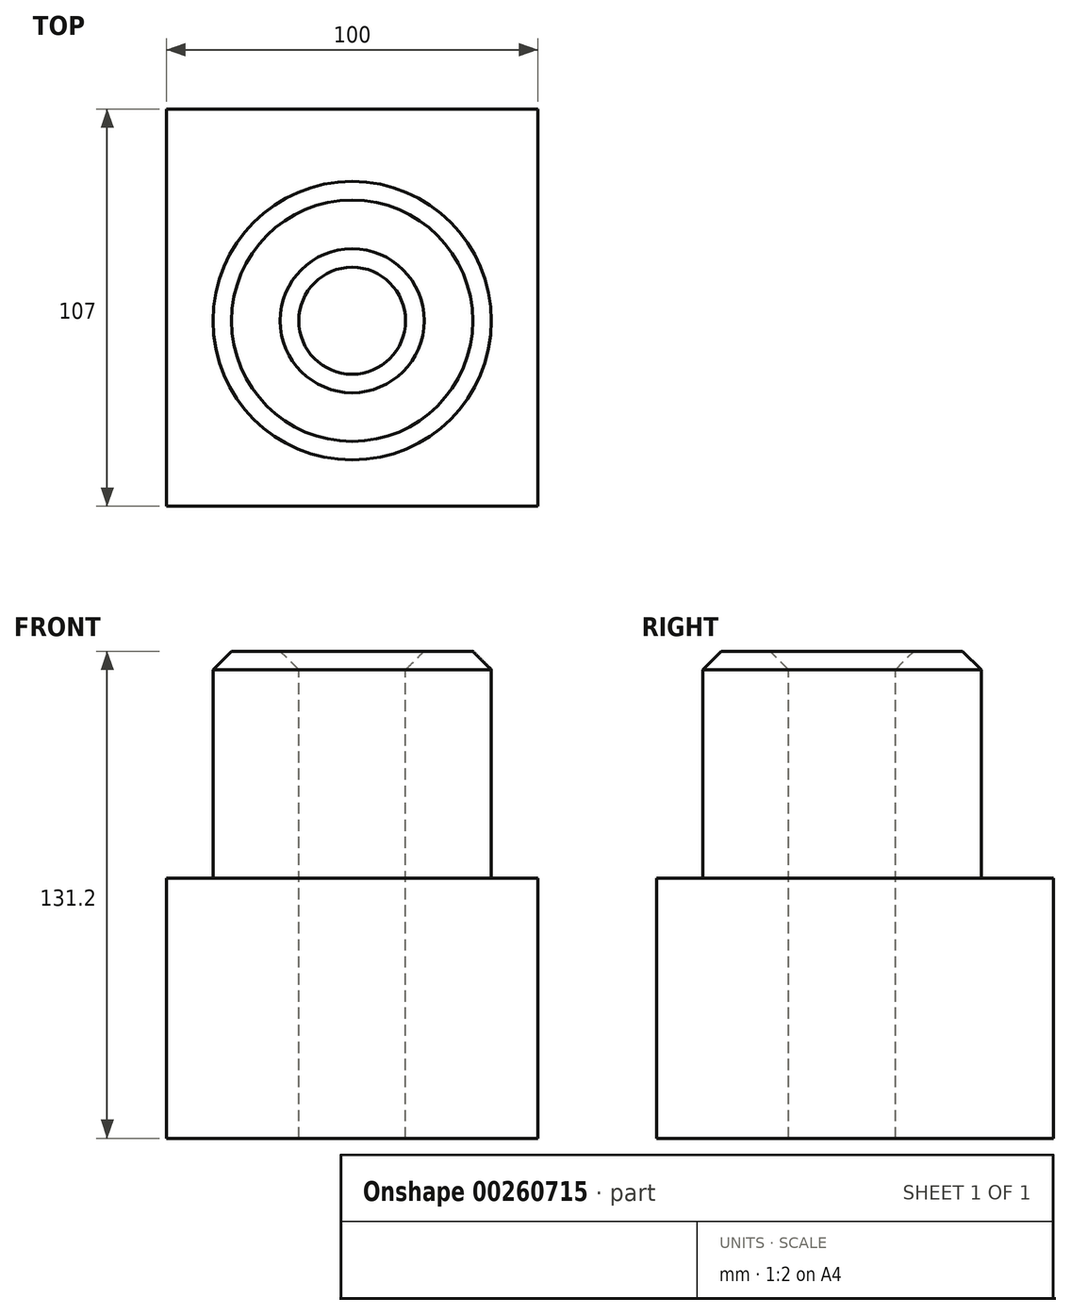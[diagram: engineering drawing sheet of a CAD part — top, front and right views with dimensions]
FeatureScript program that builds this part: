
annotation { "Feature Type Name" : "Feature", "Feature Type Description" : "" }
export const myFeature = defineFeature(function(context is Context, id is Id, definition is map)
    precondition{}
    {
        {
            var Q0;
            Q0=qCreatedBy(makeId("Front.planeOp"),FACE);
            var sketch = newSketch(context, id + "F0", { "sketchPlane" : qUnion([Q0])});
            skLineSegment(sketch, "E0.bottom", {"start": v(0, 0) * mm, "end": v(100, 0) * mm});
            skLineSegment(sketch, "E0.top", {"start": v(0, 70) * mm, "end": v(100, 70) * mm});
            skLineSegment(sketch, "E0.left", {"start": v(0, 0) * mm, "end": v(0, 70) * mm});
            skLineSegment(sketch, "E0.right", {"start": v(100, 0) * mm, "end": v(100, 70) * mm});
            skSolve(sketch);
        }
        {
            var Q0;
            Q0=qSketchRegion(id+"F0",true);
            extrude(context, id + "F1", {"entities" : qUnion([Q0]), "depth" : 107 * mm});
        }
        {
            var Q0;
            Q0=makeQuery(id+"F1.opExtrude","SWEPT_FACE",FACE,{"disambiguationData":[OSD([sQuery(id+"F0.wireOp",EDGE,"E0.top")])]});
            var sketch = newSketch(context, id + "F2", { "sketchPlane" : qUnion([Q0])});
            skCircle(sketch, "E1", {"center": v(50, -57) * mm, "radius": 37.5 * mm});
            skSolve(sketch);
        }
        {
            var Q0;
            Q0=qSketchRegion(id+"F2",true);
            extrude(context, id + "F3", {"entities" : qUnion([Q0]), "operationType" : NewBodyOperationType.ADD, "depth" : 61.2 * mm});
        }
        {
            var Q0;
            Q0=makeQuery(id+"F3.opExtrude","CAP_FACE",FACE,{"disambiguationData":[OSD([sQuery(id+"F2.wireOp",EDGE,"E1")])],"isStart":false});
            var sketch = newSketch(context, id + "F4", { "sketchPlane" : qUnion([Q0])});
            skCircle(sketch, "E2.0", {"center": v(50, -57) * mm, "radius": 14.4 * mm});
            skSolve(sketch);
        }
        {
            var Q0;
            Q0=makeQuery(id+"F4.imprint","IMPRINT",FACE,{"disambiguationData":[TD([[makeQuery(id+"F4.imprint","IMPRINT",EDGE,{"derivedFrom":sQuery(id+"F4.wireOp",EDGE,"E2.0")}),1.0]])]});
            extrude(context, id + "F5", {"entities" : qUnion([Q0]), "operationType" : NewBodyOperationType.REMOVE, "endBound" : BoundingType.THROUGH_ALL, "oppositeDirection" : true, "depth" : 25 * mm});
        }
        {
            var Q0;
            Q0=makeQuery(id+"F3.opExtrude","CAP_FACE",FACE,{"disambiguationData":[OSD([sQuery(id+"F2.wireOp",EDGE,"E1")])],"isStart":false});
            chamfer(context, id + "F6", {"entities" : qUnion([Q0]), "width" : 5 * mm, "tangentPropagation" : true});
        }
    });
